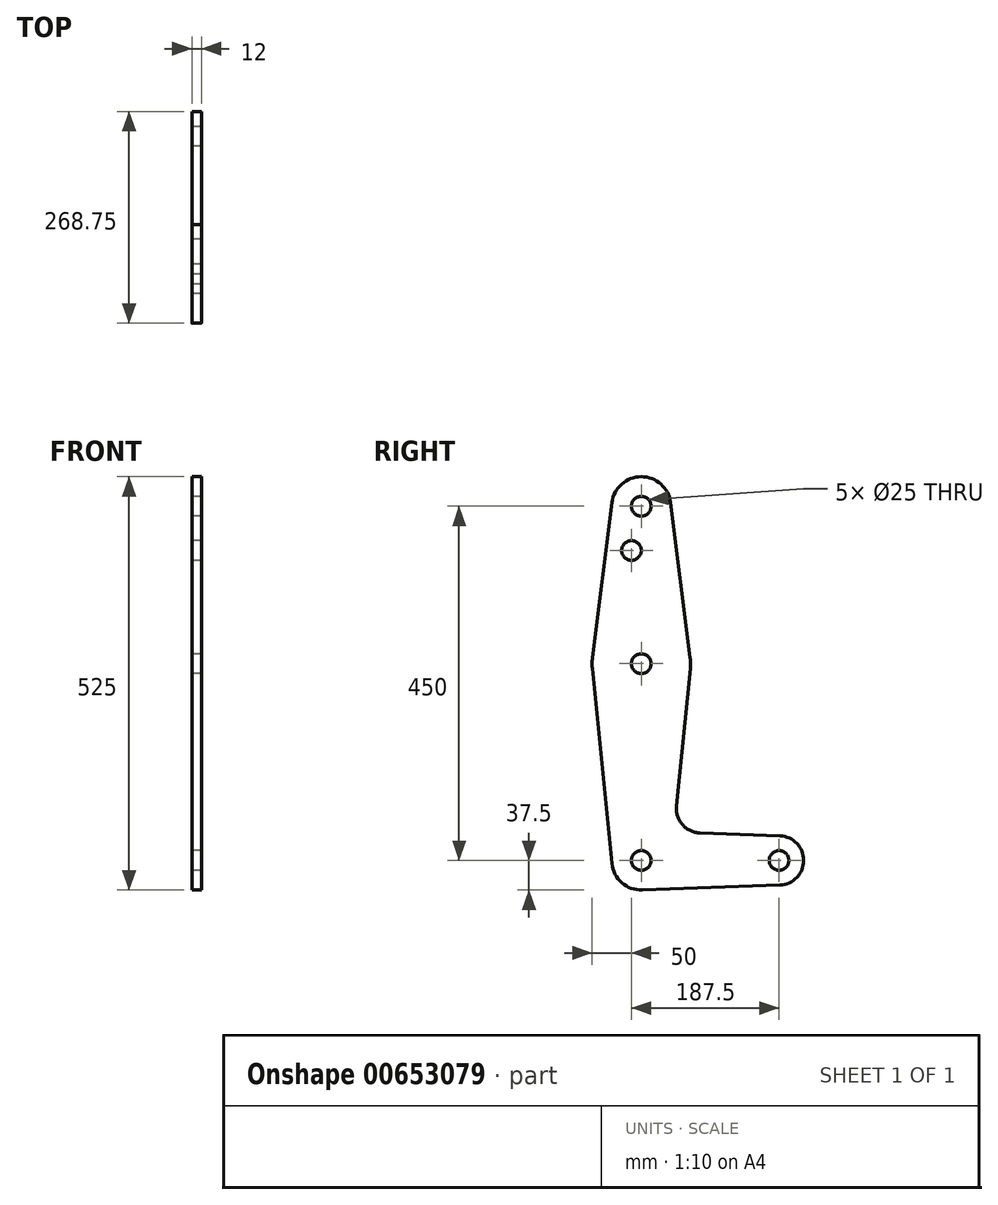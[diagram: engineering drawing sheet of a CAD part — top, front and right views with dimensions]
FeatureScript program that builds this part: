
annotation { "Feature Type Name" : "Feature", "Feature Type Description" : "" }
export const myFeature = defineFeature(function(context is Context, id is Id, definition is map)
    precondition{}
    {
        {
            var Q0;
            Q0=qCreatedBy(makeId("Right.planeOp"),FACE);
            var sketch = newSketch(context, id + "F0", { "sketchPlane" : qUnion([Q0])});
            skLineSegment(sketch, "E0", {"start": v(0, 450) * mm, "end": v(0, 0) * mm, "construction": true});
            skLineSegment(sketch, "E1", {"start": v(0, 0) * mm, "end": v(175, 0) * mm, "construction": true});
            skCircle(sketch, "E2", {"center": v(0, 450) * mm, "radius": 37.5 * mm});
            skCircle(sketch, "E3", {"center": v(0, 0) * mm, "radius": 37.5 * mm});
            skCircle(sketch, "E4", {"center": v(175, 0) * mm, "radius": 31.25 * mm});
            skCircle(sketch, "E5", {"center": v(0, 250) * mm, "radius": 62.5 * mm});
            skLineSegment(sketch, "E6", {"start": v(37.2, 454.69) * mm, "end": v(62, 257.81) * mm});
            skLineSegment(sketch, "E7", {"start": v(-37.2, 454.69) * mm, "end": v(-62, 257.81) * mm});
            skLineSegment(sketch, "E8", {"start": v(-62.19, 243.75) * mm, "end": v(-37.31, -3.75) * mm});
            skLineSegment(sketch, "E9", {"start": v(62.19, 243.75) * mm, "end": v(44.65, 69.27) * mm});
            skLineSegment(sketch, "E10", {"start": v(192.98, 30.63) * mm, "end": v(74.68, 34.86) * mm});
            skLineSegment(sketch, "E11", {"start": v(1.34, -37.48) * mm, "end": v(176.12, -31.23) * mm});
            skPoint(sketch, "E12.visualSharp", {"position": v(41.31, 36.05) * mm});
            skArc(sketch, "E12.filletArc", {"start": v(44.65, 69.27) * mm, "mid": v(52.2, 45.56) * mm, "end": v(74.68, 34.86) * mm});
            skCircle(sketch, "E13", {"center": v(0, 450) * mm, "radius": 12.5 * mm});
            skCircle(sketch, "E14", {"center": v(0, 250) * mm, "radius": 12.5 * mm});
            skCircle(sketch, "E15", {"center": v(0, 0) * mm, "radius": 12.5 * mm});
            skCircle(sketch, "E16", {"center": v(175, 0) * mm, "radius": 12.5 * mm});
            skCircle(sketch, "E17", {"center": v(-12.5, 393.8) * mm, "radius": 12.5 * mm});
            skSolve(sketch);
        }
        {
            var Q0;
            Q0 = qSketchRegion(id + "F0", true);
            extrude(context, id + "F1", {"entities" : qUnion([Q0]), "depth" : 12 * mm, "offsetDistance" : 25 * mm});
        }
    });
